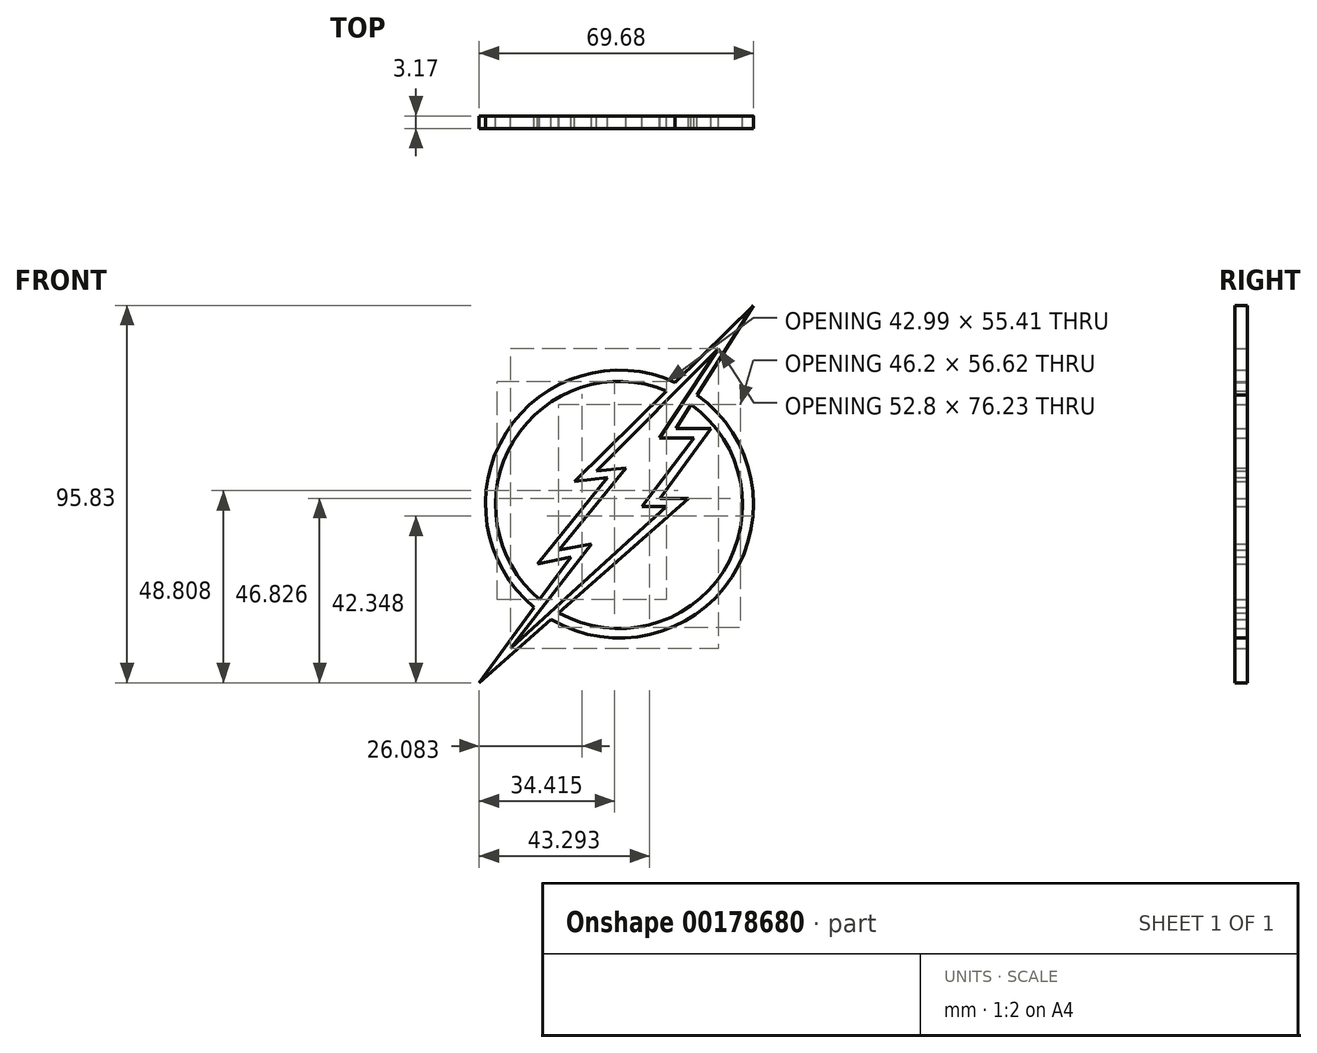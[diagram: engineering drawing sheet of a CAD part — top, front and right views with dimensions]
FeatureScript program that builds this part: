
annotation { "Feature Type Name" : "Feature", "Feature Type Description" : "" }
export const myFeature = defineFeature(function(context is Context, id is Id, definition is map)
    precondition{}
    {
        {
            var Q0;
            Q0=qCreatedBy(makeId("Front.planeOp"),FACE);
            var sketch = newSketch(context, id + "F0", { "sketchPlane" : qUnion([Q0])});
            skCircle(sketch, "E0", {"center": v(-0.18, 0.42) * mm, "radius": 31.39 * mm});
            skPoint(sketch, "E0.first.point", {"position": v(-24.78, 19.92) * mm});
            skPoint(sketch, "E0.second.point", {"position": v(30.6, 6.57) * mm});
            skPoint(sketch, "E0.third.point", {"position": v(-9.17, -29.65) * mm});
            skLineSegment(sketch, "E1", {"start": v(-27.72, -36.02) * mm, "end": v(-7.23, -9.42) * mm});
            skLineSegment(sketch, "E2", {"start": v(-7.23, -9.42) * mm, "end": v(-15.45, -11.06) * mm});
            skLineSegment(sketch, "E3", {"start": v(-15.45, -11.06) * mm, "end": v(1.62, 9.82) * mm});
            skLineSegment(sketch, "E4", {"start": v(1.62, 9.82) * mm, "end": v(-5.9, 9.08) * mm});
            skLineSegment(sketch, "E5", {"start": v(-5.9, 9.08) * mm, "end": v(25.07, 40.21) * mm});
            skLineSegment(sketch, "E6", {"start": v(25.07, 40.21) * mm, "end": v(10.03, 17.46) * mm});
            skLineSegment(sketch, "E7", {"start": v(10.03, 17.46) * mm, "end": v(18.8, 17.46) * mm});
            skLineSegment(sketch, "E8", {"start": v(18.8, 17.46) * mm, "end": v(5.63, 0) * mm});
            skLineSegment(sketch, "E9", {"start": v(5.63, 0) * mm, "end": v(11.9, 0) * mm});
            skLineSegment(sketch, "E10", {"start": v(11.9, 0) * mm, "end": v(-27.72, -36.02) * mm});
            skCircle(sketch, "E11", {"center": v(-0.1, 0.65) * mm, "radius": 34.03 * mm});
            skPoint(sketch, "E11.first.point", {"position": v(-33.17, 8.67) * mm});
            skPoint(sketch, "E11.second.point", {"position": v(32.15, -10.24) * mm});
            skPoint(sketch, "E11.third.point", {"position": v(22.13, 26.43) * mm});
            skLineSegment(sketch, "E12", {"start": v(-35.74, -44.73) * mm, "end": v(-12.44, -12.77) * mm});
            skLineSegment(sketch, "E13", {"start": v(-12.44, -12.77) * mm, "end": v(-20.92, -14.53) * mm});
            skLineSegment(sketch, "E14", {"start": v(-20.92, -14.53) * mm, "end": v(-3.17, 7.36) * mm});
            skLineSegment(sketch, "E15", {"start": v(-3.17, 7.36) * mm, "end": v(-11.56, 6.4) * mm});
            skLineSegment(sketch, "E16", {"start": v(-11.56, 6.4) * mm, "end": v(33.9, 51.1) * mm});
            skLineSegment(sketch, "E17", {"start": v(33.9, 51.1) * mm, "end": v(14.29, 19.85) * mm});
            skLineSegment(sketch, "E18", {"start": v(14.29, 19.85) * mm, "end": v(23.17, 19.85) * mm});
            skLineSegment(sketch, "E19", {"start": v(23.17, 19.85) * mm, "end": v(10.24, 2.09) * mm});
            skLineSegment(sketch, "E20", {"start": v(10.24, 2.09) * mm, "end": v(17.45, 2.09) * mm});
            skLineSegment(sketch, "E21", {"start": v(17.45, 2.09) * mm, "end": v(-35.74, -44.73) * mm});
            skSolve(sketch);
        }
        {
            var Q0;
            Q0 = qSketchRegion(id + "F0", true);
            var Q1;
            {var subQ8=sQuery(id+"F0.wireOp",EDGE,"E2");Q1=makeQuery(id+"F0.imprint","IMPRINT",FACE,{"disambiguationData":[TD([[makeQuery(id+"F0.imprint","IMPRINT",EDGE,{"derivedFrom":subQ8}),1.0]])]});}
            var Q2;
            {var subQ11=sQuery(id+"F0.wireOp",EDGE,"E7");Q2=makeQuery(id+"F0.imprint","IMPRINT",FACE,{"disambiguationData":[TD([[makeQuery(id+"F0.imprint","IMPRINT",EDGE,{"derivedFrom":subQ11}),1.0]])]});}
            extrude(context, id + "F1", {"entities" : qUnion([Q0, Q1, Q2]), "depth" : 3.17 * mm});
        }
    });
